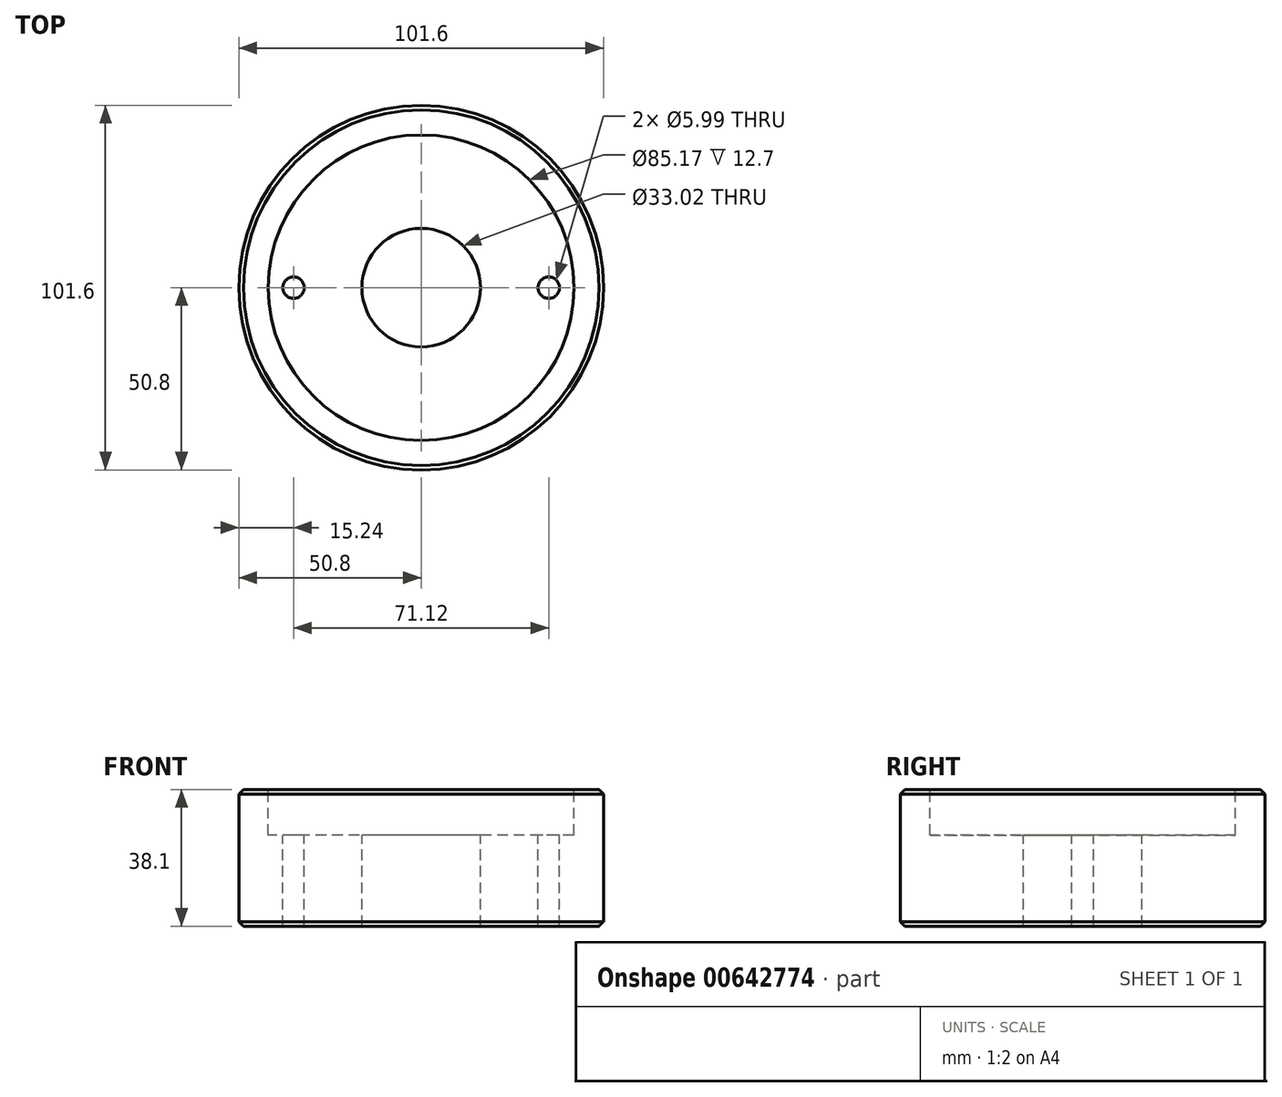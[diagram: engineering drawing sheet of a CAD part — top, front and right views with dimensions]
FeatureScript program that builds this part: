
annotation { "Feature Type Name" : "Feature", "Feature Type Description" : "" }
export const myFeature = defineFeature(function(context is Context, id is Id, definition is map)
    precondition{}
    {
        {
            var Q0;
            Q0=qCreatedBy(makeId("Top.planeOp"),FACE);
            var sketch = newSketch(context, id + "F0", { "sketchPlane" : qUnion([Q0])});
            skCircle(sketch, "E0", {"center": v(0, 0) * mm, "radius": 50.8 * mm});
            skSolve(sketch);
        }
        {
            var Q0;
            Q0 = qSketchRegion(id + "F0", true);
            extrude(context, id + "F1", {"entities" : qUnion([Q0]), "depth" : 38.1 * mm, "offsetDistance" : 25.4 * mm});
        }
        {
            var Q0;
            Q0=makeQuery(id+"F1.opExtrude","CAP_FACE",FACE,{"disambiguationData":[OSD([sQuery(id+"F0.wireOp",EDGE,"E0")])],"isStart":false});
            var sketch = newSketch(context, id + "F2", { "sketchPlane" : qUnion([Q0])});
            skCircle(sketch, "E1", {"center": v(0, 0) * mm, "radius": 42.58 * mm});
            skSolve(sketch);
        }
        {
            var Q0;
            Q0 = qSketchRegion(id + "F2", true);
            extrude(context, id + "F3", {"entities" : qUnion([Q0]), "operationType" : NewBodyOperationType.REMOVE, "oppositeDirection" : true, "depth" : 12.7 * mm, "offsetDistance" : 25.4 * mm});
        }
        {
            var Q0;
            Q0=makeQuery(id+"F3.boolean.opBoolean","COPY",FACE,{"derivedFrom":makeQuery(id+"F3.opExtrude","CAP_FACE",FACE,{"disambiguationData":[OSD([sQuery(id+"F2.wireOp",EDGE,"E1")])],"isStart":false})});
            var sketch = newSketch(context, id + "F4", { "sketchPlane" : qUnion([Q0])});
            skCircle(sketch, "E2", {"center": v(0, 0) * mm, "radius": 16.51 * mm});
            skSolve(sketch);
        }
        {
            var Q0;
            Q0 = qSketchRegion(id + "F4", true);
            extrude(context, id + "F5", {"entities" : qUnion([Q0]), "operationType" : NewBodyOperationType.REMOVE, "endBound" : BoundingType.THROUGH_ALL, "oppositeDirection" : true, "depth" : 25.4 * mm, "offsetDistance" : 25.4 * mm});
        }
        {
            var Q0;
            Q0=makeQuery(id+"F3.boolean.opBoolean","COPY",EDGE,{"derivedFrom":makeQuery(id+"F3.opExtrude","CAP_EDGE",EDGE,{"disambiguationData":[OSD([sQuery(id+"F2.wireOp",EDGE,"E1")])],"isStart":true})});
            var Q1;
            Q1=makeQuery(id+"F5.boolean.opBoolean","COPY",EDGE,{"derivedFrom":makeQuery(id+"F5.opExtrude","CAP_EDGE",EDGE,{"disambiguationData":[OSD([sQuery(id+"F4.wireOp",EDGE,"E2")])],"isStart":true})});
            var Q2;
            Q2=makeQuery(id+"F1.opExtrude","CAP_EDGE",EDGE,{"disambiguationData":[OSD([sQuery(id+"F0.wireOp",EDGE,"E0")])],"isStart":false});
            var Q3;
            Q3=makeQuery(id+"F1.opExtrude","CAP_EDGE",EDGE,{"disambiguationData":[OSD([sQuery(id+"F0.wireOp",EDGE,"E0")])],"isStart":true});
            chamfer(context, id + "F6", {"entities" : qUnion([Q0, Q1, Q2, Q3]), "width" : 1.27 * mm, "tangentPropagation" : true});
        }
        {
            var Q0;
            Q0=makeQuery(id+"F3.boolean.opBoolean","COPY",FACE,{"derivedFrom":makeQuery(id+"F3.opExtrude","CAP_FACE",FACE,{"disambiguationData":[OSD([sQuery(id+"F2.wireOp",EDGE,"E1")])],"isStart":false})});
            var sketch = newSketch(context, id + "F7", { "sketchPlane" : qUnion([Q0])});
            skCircle(sketch, "E3", {"center": v(35.56, 0) * mm, "radius": 3 * mm});
            skCircle(sketch, "E4", {"center": v(-35.56, 0) * mm, "radius": 3 * mm});
            skSolve(sketch);
        }
        {
            var Q0;
            Q0 = qSketchRegion(id + "F7", true);
            extrude(context, id + "F8", {"entities" : qUnion([Q0]), "operationType" : NewBodyOperationType.REMOVE, "endBound" : BoundingType.THROUGH_ALL, "oppositeDirection" : true, "depth" : 25.4 * mm, "offsetDistance" : 25.4 * mm});
        }
    });
